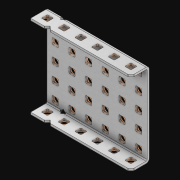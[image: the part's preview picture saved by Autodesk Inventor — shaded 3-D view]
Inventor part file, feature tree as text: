
AUTODESK INVENTOR PART (.ipt)
format: ipt  version: 2021 (Build 250183000, 183)  size: 2,931,200 bytes
history: native  units: in
note: dims shown in document units (in); Inventor stores cm internally (conversion verified against a paired STEP export)
features: extrude x43, other x42, sketch x4, thicken_offset x3, pattern_linear x3, imported_body x1
ambient origin geometry x8: Origin, YZ Plane, XZ Plane, XY Plane, X Axis, Y Axis, Z Axis, Center Point
bodies: Solid1 (feature_tree)
feature tree (96):
  thicken_offset  "Thicken1"
  thicken_offset  "Thicken2"
  thicken_offset  "Thicken3"
  pattern_linear  "Rectangular Pattern1"  Spacing1=0.001in  [1 undecoded]
  pattern_linear  "Rectangular Pattern2"  Spacing1=0.001in  [1 undecoded]
  pattern_linear  "Rectangular Pattern3"  Spacing1=0.182in  [1 undecoded]
  extrude  "Extrusion1"  Depth=0.063in TaperAngle=0.0deg
  sketch  "Sketch1"  dims[d0=0.001in]
  other  "Srf1"
  sketch  "Sketch2"  dims[d1=0.001in]
  other  "Srf2"
  sketch  "Sketch3"  dims[d2=0.001in]
  other  "Srf3"
  other  "Srf4"
  other  "Srf5"
  other  "Srf6"
  other  "Srf7"
  other  "Srf8"
  other  "Srf38"
  other  "Srf39"
  other  "Srf40"
  other  "Srf41"
  other  "Srf42"
  other  "Srf72"
  other  "Srf73"
  other  "Srf74"
  other  "Srf75"
  other  "Srf76"
  other  "Srf106"
  other  "Srf107"
  other  "Srf108"
  other  "Srf109"
  other  "Srf110"
  other  "Srf111"
  other  "Srf141"
  other  "Srf142"
  other  "Srf143"
  other  "Srf144"
  other  "Srf145"
  other  "Srf146"
  other  "Srf176"
  other  "Srf177"
  other  "Srf178"
  other  "Srf179"
  other  "Srf180"
  other  "Srf181"
  other  "Srf211"
  other  "Srf212"
  other  "Srf213"
  other  "Srf214"
  other  "Srf215"
  other  "Srf216"
  sketch  "Sketch4"  dims[d3=0.001in d4=0.001in d5=0.001in d6=0.182in d7=0.063in d8=0.0in d9=0.182in d10=0.063in d11=0.0in d12=0.182in d13=0.063in d14=0.0in d17=0.5in d18=2.3622in d20=0.5in d21=2.3622in d23=0.5in d24=1.9685in d26=0.5in d27=14.5in d28=0.0in]
  imported_body  "Imported1"
  extrude  "ExtrusionSrf1"  Depth=0.063in
  extrude  "ExtrusionSrf2"  Depth=0.063in TaperAngle=0.0deg
  extrude  "ExtrusionSrf3"  Depth=0.063in
  extrude  "ExtrusionSrf4"  Depth=0.063in TaperAngle=0.0deg
  extrude  "ExtrusionSrf5"  Depth=0.063in
  extrude  "ExtrusionSrf6"  Depth=0.063in
  extrude  "ExtrusionSrf7"  Depth=0.063in
  extrude  "ExtrusionSrf8"  Depth=0.063in
  extrude  "ExtrusionSrf38"  Depth=0.063in
  extrude  "ExtrusionSrf39"  Depth=0.063in
  extrude  "ExtrusionSrf40"  Depth=0.063in
  extrude  "ExtrusionSrf41"  TaperAngle=0.0deg  [1 undecoded]
  extrude  "ExtrusionSrf42"  [1 undecoded]
  extrude  "ExtrusionSrf72"  [1 undecoded]
  extrude  "ExtrusionSrf73"  [1 undecoded]
  extrude  "ExtrusionSrf74"  [1 undecoded]
  extrude  "ExtrusionSrf75"  [1 undecoded]
  extrude  "ExtrusionSrf76"  [1 undecoded]
  extrude  "ExtrusionSrf106"  [1 undecoded]
  extrude  "ExtrusionSrf107"  [1 undecoded]
  extrude  "ExtrusionSrf108"  [1 undecoded]
  extrude  "ExtrusionSrf109"  [1 undecoded]
  extrude  "ExtrusionSrf110"  [1 undecoded]
  extrude  "ExtrusionSrf111"  [1 undecoded]
  extrude  "ExtrusionSrf141"  [1 undecoded]
  extrude  "ExtrusionSrf142"  [1 undecoded]
  extrude  "ExtrusionSrf143"  [1 undecoded]
  extrude  "ExtrusionSrf144"  [1 undecoded]
  extrude  "ExtrusionSrf145"  [1 undecoded]
  extrude  "ExtrusionSrf146"  [1 undecoded]
  extrude  "ExtrusionSrf176"  [1 undecoded]
  extrude  "ExtrusionSrf177"  [1 undecoded]
  extrude  "ExtrusionSrf178"  [1 undecoded]
  extrude  "ExtrusionSrf179"  [1 undecoded]
  extrude  "ExtrusionSrf180"  [1 undecoded]
  extrude  "ExtrusionSrf181"  [1 undecoded]
  extrude  "ExtrusionSrf211"  [1 undecoded]
  extrude  "ExtrusionSrf212"  [1 undecoded]
  extrude  "ExtrusionSrf213"  [1 undecoded]
  extrude  "ExtrusionSrf214"  [1 undecoded]
  extrude  "ExtrusionSrf215"  [1 undecoded]
  extrude  "ExtrusionSrf216"  [1 undecoded]
note: 34 required parameter values undecoded (feature->parameter linkage not recoverable at this tier; creation-order binding heuristic only, values carry confidence <= 0.55)
